# Revit family: QF_COMCATER ALL BRANDS_RCR6-6G
name_source: partatom
category: Specialty Equipment
revit_build: Autodesk Revit 2014 (Build: 20140709_2115(x64)
units: mm (PartAtom-declared; Revit-internal decimal feet)

## types (2) — shared parameters
Accessory = No
Assembly Code = E1090320
BTUH = 13800 W
Depth Actual = 830 mm  [stored 2.7231 ft]
Description = GRIDDLE RANGE WITH OVEN
Gas Flow = 0.0 L/s
Gas Size = 19 mm
Gas Size Flexible = 0 mm
Gas power kW = 13.8
Height Actual = 1135 mm  [stored 3.72375 ft]
Length Actual = 600 mm  [stored 1.9685 ft]
Manufacturer = TRUEHEAT
Model = RCR6-6G
Nominal Gas power = 13800 W
Type Comments = The Australian owned and designed* Trueheat RC Series of Gas Cooking Equipment has been developed for the restaurant and cafe market with a high quality finish, designed to fulfill the busy demands within a commercial kitchen.
16mm thick steel griddle plate with 16.5MJ/hr burner per 300mm section.
100% Flame failure controls included as standard. Piezo ignition on enclosed oven burners. Matt finish premium look.
25MJ/hr static oven with two oven racks fit to removable vertical rack guides which provide 3 rack heights. Oven racks are fabricated from 304 stainless steel. Interior oven panels are coated with black vitreous enamel for ease of cleaning.

## type names (no varying parameters)
- RCR6-6G_Natural Gas
- RCR6-6G_LPG

note: [stored X ft] marks values corroborated as IEEE doubles in the binary element streams (Revit-internal decimal feet)

## geometry (parser evidence)
native form markers: Sweep x5
no freeform markers — native parametric forms only
